# Revit family: PRD_FrankeWS_PllrTps_AQUAMIXZeroSelf-closingPillarMixer_AQRM176
name_source: partatom
category: Plumbing Fixtures
revit_build: Autodesk Revit 2018 (Build: 20190510_1515(x64)
units: mm (PartAtom-declared; Revit-internal decimal feet)

## family parameters
Always vertical = Yes
Cut with Voids When Loaded = No
OmniClass Number = 23.45.55.17
OmniClass Title = Mixing Faucets
Part Type = Normal
Room Calculation Point = No
Round Connector Dimension = Use Diameter
Shared = No
Work Plane-Based = Yes

## types (1)
- AQRM176
    AdjustableFlowTime = Yes
    AssetType = Fixed
    BIMObjectName = PRD_AR_PillarTaps_AQUAMIXZeroSelf-closingPillarMixer_AQRM176
    CalculationFlowRateColdWater = 0.07 liter per second
    Category = Pr_40_20_87_60, Pillar taps
    Color = Chrome
    Default Elevation = 0 mm  [stored 0 ft]
    Depressurised = Yes
    Description = AQUAMIX ZERO self-closing single mixer DN 15 as pillar mixer, with open low-level domestic hot water heaters, for open low-level domestic hot water heaters, flow time adjustable, polished chromium-plated brass, with grip cap or lever cap in metal construction. With grip cap.
    DiameterNominal = 15 mm
    DurationUnit = year
    FaucetFunction = Mixed
    FaucetOperation = TimedSelfClosing
    FaucetType = Pillar
    Features = For open low-level domestic hot water heaters, polished chromium-plated brass.
    Finish = Polished chrome
    FlowColdWater = 0.1 L/s
    FlowRateMaximum = 0.08 L/s at 3 bar
    FunctionalPrinciple = Hydraulic self-closing
    GrossWeight = 3.16 kg
    HygieneFlushing = No
    IfcExportAs = IfcValveType
    IfcExportType = FAUCET
    InletSize = DN 15
    IntegralAccessories = With grip cap
    MainMaterial = PRD_AR_ChromatedBrass_HighPolished
    Manufacturer = KWC Group AG
    ManufacturerName = KWC Group AG
    ManufacturerURL = www.kwc.com
    Material = Brass
    MaximumFlowTime = 15.00 seconds
    MinimumFlowPressure = 1.00 bar
    MinimumFlowTime = 1.00 seconds
    Model = AQRM176
    ModelNumber = 2000101062
    ModelReference = AQRM176
    Name = AQUAMIX ZERO self-closing pillar mixer for hot water heaters AQRM176
    NetWeight = 2.87 kg
    NominalDepth = 0 mm  [stored 0 ft]
    NominalHeight = 146 mm  [stored 0.479003 ft]
    NominalWidth = 0 mm  [stored 0 ft]
    ProductCode = 208.0637.547
    ProductInformation = https://pim.kwc.com
    ProtectiveShutdown = No
    Shape = Pillar
    SoundInsulation = No
    SpoutProjection = 90.00 mm
    ThermalDisinfection = No
    TypeOfMixing = With mixing
    TypeOfMounting = Tap hole
    TypeOfOperation = Manual operation
    TypeOfTap = Pillar tap
    URL = www.kwc.com
    Uniclass2015Code = Pr_40_20_87_60
    Uniclass2015Title = Pillar taps
    Uniclass2015Version = Products v1.17
    Version = 1
    WarrantyDurationUnit = year

note: [stored X ft] marks values corroborated as IEEE doubles in the binary element streams (Revit-internal decimal feet)

## geometry (parser evidence)
native form markers: Sweep x6
no freeform markers — native parametric forms only
